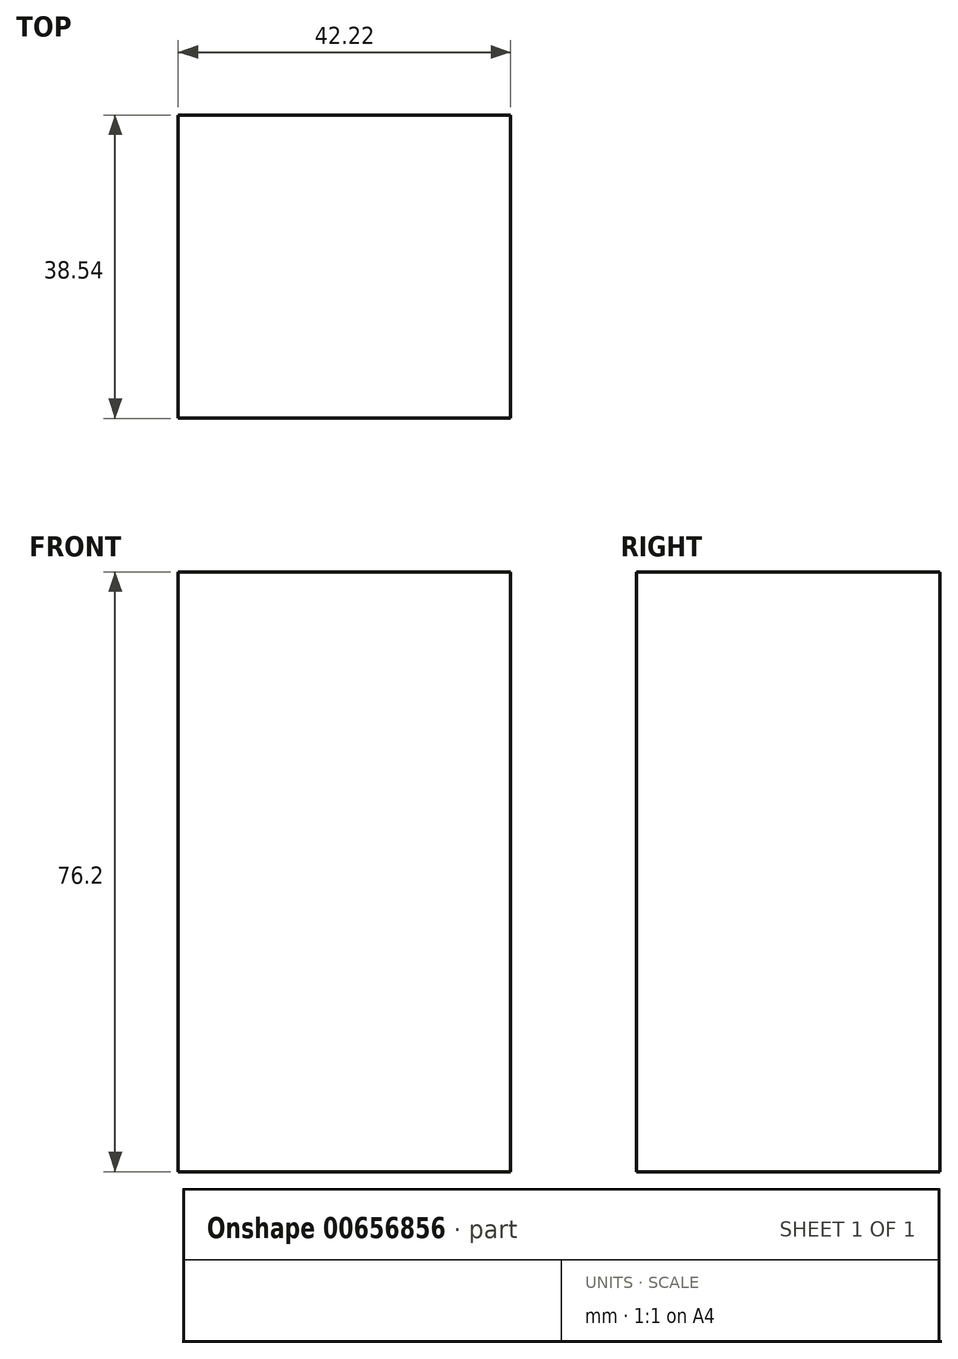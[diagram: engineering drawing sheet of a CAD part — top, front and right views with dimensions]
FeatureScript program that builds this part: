
annotation { "Feature Type Name" : "Feature", "Feature Type Description" : "" }
export const myFeature = defineFeature(function(context is Context, id is Id, definition is map)
    precondition{}
    {
        {
            var Q0;
            Q0=qCreatedBy(makeId("Top.planeOp"),FACE);
            var sketch = newSketch(context, id + "F0", { "sketchPlane" : qUnion([Q0])});
            skLineSegment(sketch, "E0.bottom", {"start": v(-21.1, 19.27) * mm, "end": v(21.1, 19.27) * mm});
            skLineSegment(sketch, "E0.top", {"start": v(-21.1, -19.27) * mm, "end": v(21.1, -19.27) * mm});
            skLineSegment(sketch, "E0.left", {"start": v(-21.1, 19.27) * mm, "end": v(-21.1, -19.27) * mm});
            skLineSegment(sketch, "E0.right", {"start": v(21.1, 19.27) * mm, "end": v(21.1, -19.27) * mm});
            skPoint(sketch, "E0.middle", {"position": v(0, 0) * mm});
            skSolve(sketch);
        }
        {
            var Q0;
            Q0=makeQuery(id+"F0.imprint","IMPRINT",FACE,{"disambiguationData":[TD([[makeQuery(id+"F0.imprint","IMPRINT",EDGE,{"derivedFrom":sQuery(id+"F0.wireOp",EDGE,"E0.bottom")}),-1.0]])]});
            extrude(context, id + "F1", {"entities" : qUnion([Q0]), "depth" : 76.2 * mm, "offsetDistance" : 25.4 * mm});
        }
    });
